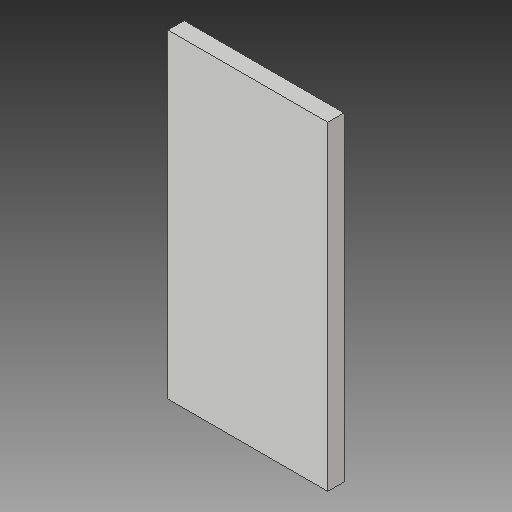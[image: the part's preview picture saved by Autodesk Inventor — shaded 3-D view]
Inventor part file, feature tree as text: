
AUTODESK INVENTOR PART (.ipt)
format: ipt  version: 2018 (Build 220112000, 112)  size: 91,648 bytes
history: native  units: mm
features: other x1, extrude x1, sketch x1
ambient origin geometry x8: Origin, YZ Plane, XZ Plane, XY Plane, X Axis, Y Axis, Z Axis, Center Point
bodies: Body1 (feature_tree)
feature tree (3):
  other  "Sólido1"
  extrude  "Extrusão1"  Depth=250.0mm
  sketch  "Esboço1"  dims[d0=125.0mm d1=250.0mm d2=12.7mm d3=0.0mm]
